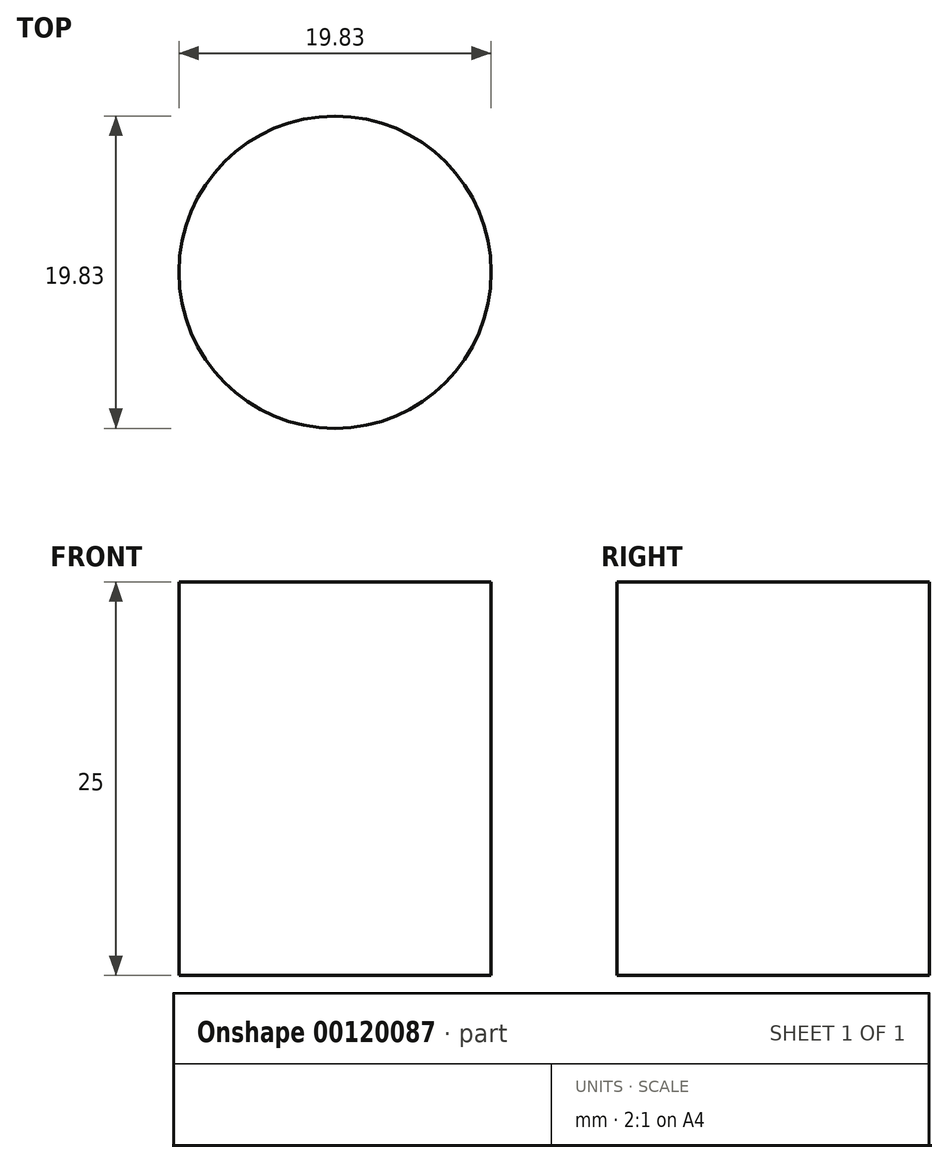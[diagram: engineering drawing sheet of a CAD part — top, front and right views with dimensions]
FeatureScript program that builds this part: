
annotation { "Feature Type Name" : "Feature", "Feature Type Description" : "" }
export const myFeature = defineFeature(function(context is Context, id is Id, definition is map)
    precondition{}
    {
        {
            var Q0;
            Q0=qCreatedBy(makeId("Top.planeOp"),FACE);
            var sketch = newSketch(context, id + "F0", { "sketchPlane" : qUnion([Q0])});
            skCircle(sketch, "E0", {"center": v(-24.71, 17.47) * mm, "radius": 9.92 * mm});
            skSolve(sketch);
        }
        {
            var Q0;
            Q0=sQuery(id+"F0.wireOp",EDGE,"E0");
            extrude(context, id + "F1", {"bodyType" : ToolBodyType.SURFACE, "surfaceEntities" : qUnion([Q0]), "depth" : 25 * mm});
        }
    });
